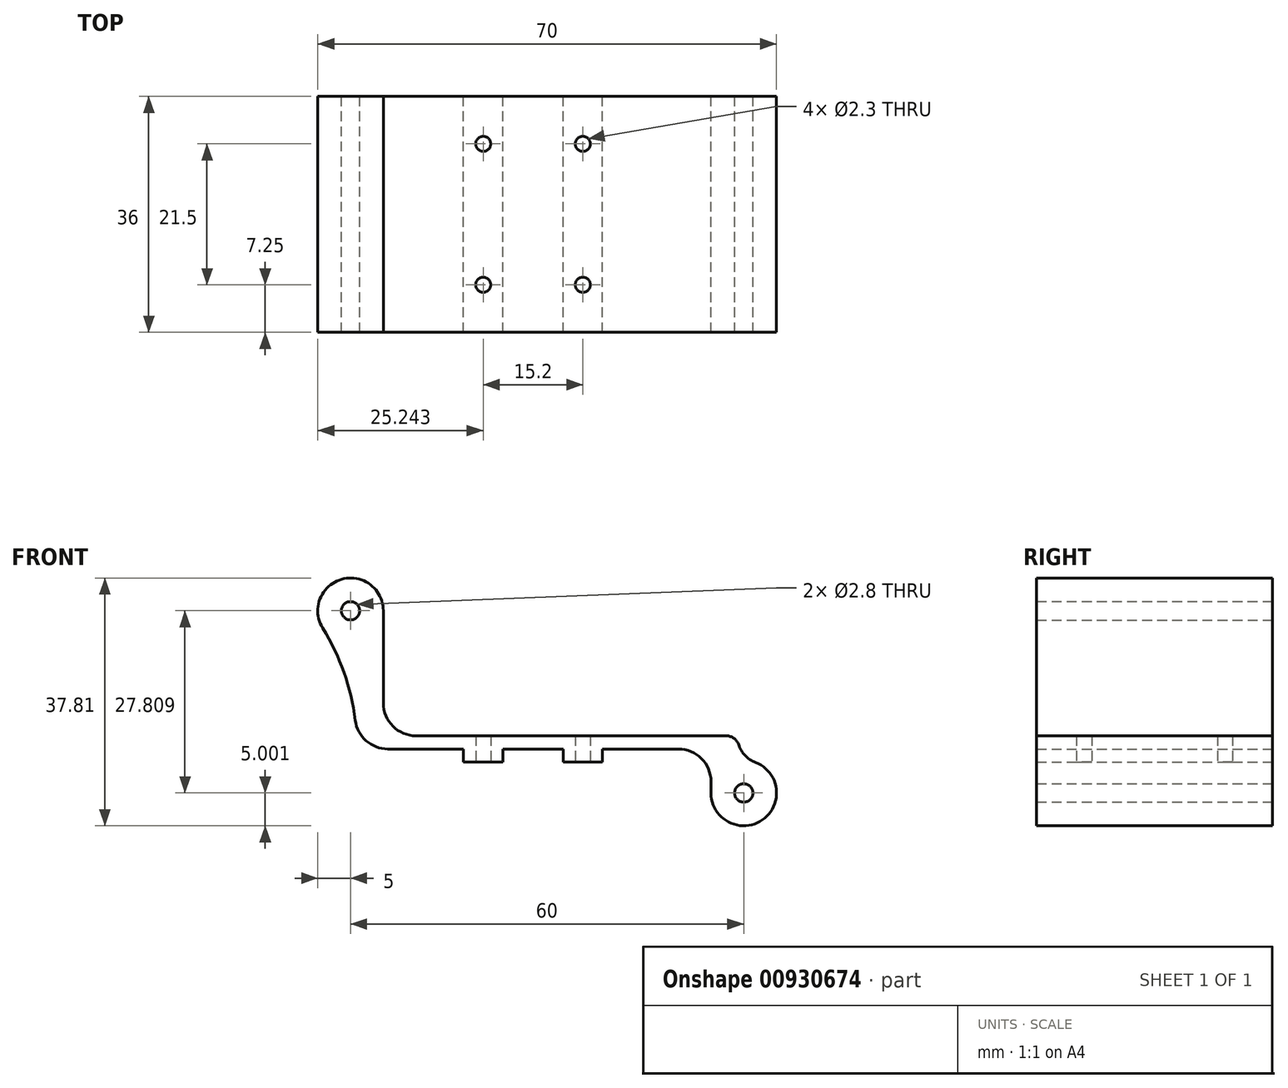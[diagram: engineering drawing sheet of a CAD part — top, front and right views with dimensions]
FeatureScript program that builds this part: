
annotation { "Feature Type Name" : "Feature", "Feature Type Description" : "" }
export const myFeature = defineFeature(function(context is Context, id is Id, definition is map)
    precondition{}
    {
        {
            var Q0;
            Q0=qCreatedBy(makeId("Front.planeOp"),FACE);
            var sketch = newSketch(context, id + "F0", { "sketchPlane" : qUnion([Q0])});
            skCircle(sketch, "E0", {"center": v(0, 0) * mm, "radius": 1.4 * mm});
            skCircle(sketch, "E1", {"center": v(60, -27.8) * mm, "radius": 1.4 * mm});
            skCircle(sketch, "E2", {"center": v(35, -55.09) * mm, "radius": 29 * mm, "construction": true});
            skArc(sketch, "E3", {"start": v(55, -27.8) * mm, "mid": v(62.83, -31.93) * mm, "end": v(61.79, -23.14) * mm});
            skLineSegment(sketch, "E4", {"start": v(1, -21.09) * mm, "end": v(55, -21.09) * mm});
            skLineSegment(sketch, "E5", {"start": v(55, -21.09) * mm, "end": v(55, -27.8) * mm});
            skArc(sketch, "E6", {"start": v(1, -21.09) * mm, "mid": v(-0.34, -11.5) * mm, "end": v(-4.25, -2.63) * mm});
            skArc(sketch, "E7", {"start": v(59, -19.09) * mm, "mid": v(59.76, -21.55) * mm, "end": v(61.79, -23.14) * mm});
            skLineSegment(sketch, "E8", {"start": v(5, -19.09) * mm, "end": v(5, 0) * mm});
            skLineSegment(sketch, "E9.trimOffspring", {"start": v(5, -19.09) * mm, "end": v(59, -19.09) * mm});
            skArc(sketch, "E10.trimOffspring", {"start": v(5, 0) * mm, "mid": v(-1.37, 4.8) * mm, "end": v(-4.25, -2.63) * mm});
            skSolve(sketch);
        }
        {
            var Q0;
            Q0=qSketchRegion(id+"F0",true);
            extrude(context, id + "F1", {"entities" : qUnion([Q0]), "depth" : 36 * mm});
        }
        {
            var Q0;
            Q0=makeQuery(id+"F1.opExtrude","SWEPT_EDGE",EDGE,{"disambiguationData":[OSD([sQuery(id+"F0.wireOp",EDGE,"E8"),sQuery(id+"F0.wireOp",EDGE,"E9.trimOffspring")])]});
            var Q1;
            Q1=makeQuery(id+"F1.opExtrude","SWEPT_EDGE",EDGE,{"disambiguationData":[OSD([sQuery(id+"F0.wireOp",EDGE,"E4"),sQuery(id+"F0.wireOp",EDGE,"E6")])]});
            var Q2;
            Q2=makeQuery(id+"F1.opExtrude","SWEPT_EDGE",EDGE,{"disambiguationData":[OSD([sQuery(id+"F0.wireOp",EDGE,"E4"),sQuery(id+"F0.wireOp",EDGE,"E5")])]});
            fillet(context, id + "F2", {"entities" : qUnion([Q0, Q1, Q2]), "radius" : 5 * mm, "tangentPropagation" : true, "allowEdgeOverflow" : false});
        }
        {
            var Q0;
            Q0=makeQuery(id+"F1.opExtrude","SWEPT_FACE",FACE,{"disambiguationData":[OSD([sQuery(id+"F0.wireOp",EDGE,"E4")])]});
            var sketch = newSketch(context, id + "F3", { "sketchPlane" : qUnion([Q0])});
            skLineSegment(sketch, "E11", {"start": v(5.69, 18) * mm, "end": v(50, 18) * mm, "construction": true});
            skLineSegment(sketch, "E12", {"start": v(27.84, 36) * mm, "end": v(27.84, 0) * mm, "construction": true});
            skLineSegment(sketch, "E13.bottom", {"start": v(17.64, 31.5) * mm, "end": v(38.04, 31.5) * mm, "construction": true});
            skLineSegment(sketch, "E13.top", {"start": v(17.64, 4.5) * mm, "end": v(38.04, 4.5) * mm, "construction": true});
            skLineSegment(sketch, "E13.left", {"start": v(17.64, 31.5) * mm, "end": v(17.64, 4.5) * mm, "construction": true});
            skLineSegment(sketch, "E13.right", {"start": v(38.04, 31.5) * mm, "end": v(38.04, 4.5) * mm, "construction": true});
            skCircle(sketch, "E14", {"center": v(20.24, 28.75) * mm, "radius": 3 * mm, "construction": true});
            skCircle(sketch, "E15", {"center": v(35.44, 28.75) * mm, "radius": 3 * mm, "construction": true});
            skCircle(sketch, "E16", {"center": v(20.24, 7.25) * mm, "radius": 3 * mm, "construction": true});
            skCircle(sketch, "E17", {"center": v(35.44, 7.25) * mm, "radius": 3 * mm, "construction": true});
            skLineSegment(sketch, "E18.bottom", {"start": v(17.24, 36) * mm, "end": v(23.24, 36) * mm});
            skLineSegment(sketch, "E18.top", {"start": v(17.24, 0) * mm, "end": v(23.24, 0) * mm});
            skLineSegment(sketch, "E18.left", {"start": v(17.24, 36) * mm, "end": v(17.24, 0) * mm});
            skLineSegment(sketch, "E18.right", {"start": v(23.24, 36) * mm, "end": v(23.24, 0) * mm});
            skLineSegment(sketch, "E19.bottom", {"start": v(32.44, 36) * mm, "end": v(38.44, 36) * mm});
            skLineSegment(sketch, "E19.top", {"start": v(32.44, 0) * mm, "end": v(38.44, 0) * mm});
            skLineSegment(sketch, "E19.left", {"start": v(32.44, 36) * mm, "end": v(32.44, 0) * mm});
            skLineSegment(sketch, "E19.right", {"start": v(38.44, 36) * mm, "end": v(38.44, 0) * mm});
            skSolve(sketch);
        }
        {
            var Q0;
            Q0=qSketchRegion(id+"F3",true);
            extrude(context, id + "F4", {"entities" : qUnion([Q0]), "operationType" : NewBodyOperationType.ADD, "depth" : 2 * mm});
        }
        {
            var Q0;
            Q0=makeQuery(id+"F1.opExtrude","SWEPT_EDGE",EDGE,{"disambiguationData":[OSD([sQuery(id+"F0.wireOp",EDGE,"E7"),sQuery(id+"F0.wireOp",EDGE,"E9.trimOffspring")])]});
            fillet(context, id + "F5", {"entities" : qUnion([Q0]), "radius" : 2 * mm, "tangentPropagation" : true, "allowEdgeOverflow" : false});
        }
        {
            var Q0;
            Q0=makeQuery(id+"F4.opExtrude","CAP_FACE",FACE,{"disambiguationData":[OSD([sQuery(id+"F3.wireOp",EDGE,"E18.bottom"),sQuery(id+"F3.wireOp",EDGE,"E18.top"),sQuery(id+"F3.wireOp",EDGE,"E18.left"),sQuery(id+"F3.wireOp",EDGE,"E18.right")])],"isStart":false});
            var sketch = newSketch(context, id + "F6", { "sketchPlane" : qUnion([Q0])});
            skLineSegment(sketch, "E20", {"start": v(17.24, 18) * mm, "end": v(38.44, 18) * mm, "construction": true});
            skCircle(sketch, "E21", {"center": v(20.24, 28.75) * mm, "radius": 1.15 * mm});
            skCircle(sketch, "E22", {"center": v(35.44, 28.75) * mm, "radius": 1.15 * mm});
            skCircle(sketch, "E23", {"center": v(20.24, 7.25) * mm, "radius": 1.15 * mm});
            skCircle(sketch, "E24", {"center": v(35.44, 7.25) * mm, "radius": 1.15 * mm});
            skSolve(sketch);
        }
        {
            var Q0;
            Q0=qSketchRegion(id+"F6",true);
            extrude(context, id + "F7", {"entities" : qUnion([Q0]), "operationType" : NewBodyOperationType.REMOVE, "endBound" : BoundingType.UP_TO_NEXT, "oppositeDirection" : true, "depth" : 25 * mm, "offsetDistance" : 25 * mm});
        }
    });
